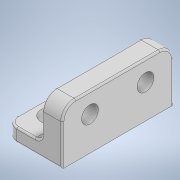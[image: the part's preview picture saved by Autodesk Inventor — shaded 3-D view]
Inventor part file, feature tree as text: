
AUTODESK INVENTOR PART (.ipt)
format: ipt  version: 2021.3 (Build 253353010, 353A)  size: 221,184 bytes
history: native  units: mm
features: sketch x5, extrude x3, fillet x3, hole x1, projected_geometry x1
ambient origin geometry x8: Origin, YZ Plane, XZ Plane, XY Plane, X Axis, Y Axis, Z Axis, Center Point
bodies: Volumenkörper1 (feature_tree)
feature tree (13):
  extrude  "Extrusion1"  Depth=2.0mm
  extrude  "Extrusion2"  Depth=10.0mm
  sketch  "Skizze4"  dims[d4=3.0mm d5=4.0mm d6=0.0mm d8=6.0mm d9=0.0mm d21=12.0mm]
  hole  "Bohrung1"  [1 undecoded]
  fillet  "Rundung1"  Radius=6.0mm
  fillet  "Rundung2"  Radius=12.0mm
  fillet  "Rundung3"  Radius=2.0mm
  extrude  "Extrusion3"  Depth=2.0mm
  sketch  "Skizze1"  dims[d0=2.0mm d1=6.5mm]
  sketch  "Skizze3"  dims[d2=5.0mm d3=10.0mm]
  sketch  "Skizze5"  dims[d22=5.0mm d23=8.60806mm d24=8.6mm d25=2.0mm d26=90.0deg d27=8.0mm d28=20.594885mm d29=2.0mm]
  projected_geometry  "Projizierte Kontur1"
  sketch  "Skizze7"  dims[d30=4.0mm d31=0.5mm d32=2.0mm d33=12.0mm d34=0.0mm]
note: 1 required parameter value undecoded (feature->parameter linkage not recoverable at this tier; creation-order binding heuristic only, values carry confidence <= 0.55)
